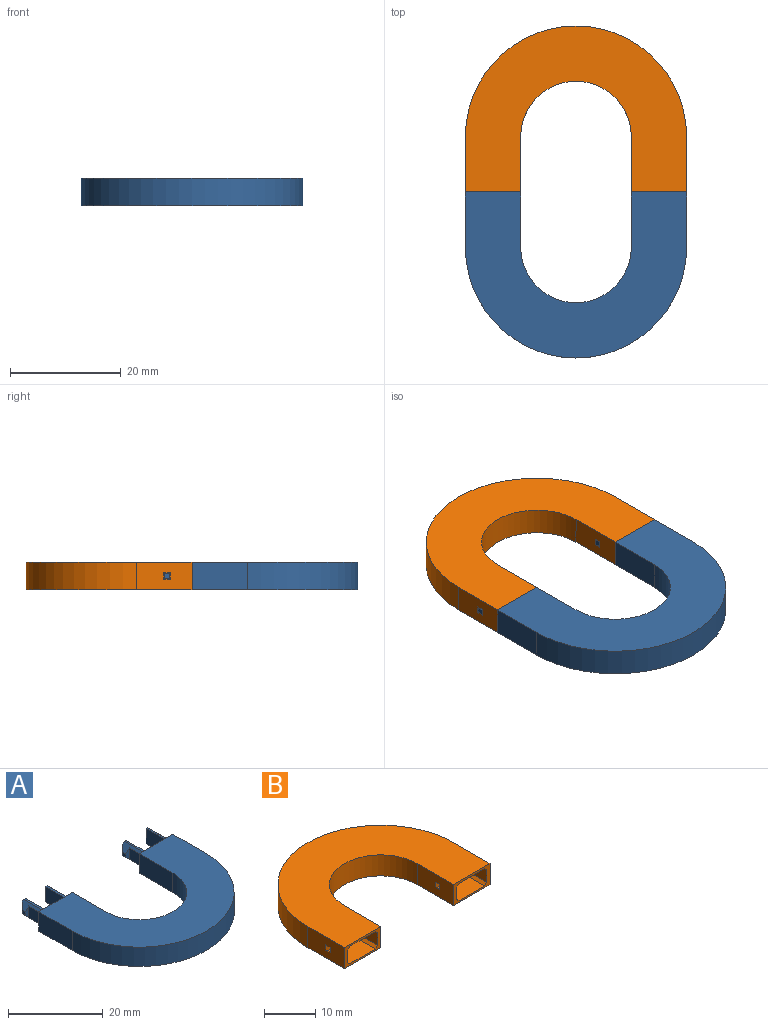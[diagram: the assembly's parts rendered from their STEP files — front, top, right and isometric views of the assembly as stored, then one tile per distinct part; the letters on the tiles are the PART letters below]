
ASSEMBLY  parts=2 mates=1
PART A: 50 faces, bbox 40x36x5 mm
  f0: plane 3.95x1mm, normal (0,1,0), area 3.7mm2, adj f9,f31,f46,f47,f48,f49
  f1: plane 1x1mm, normal (-1,0,0), area 1mm2, adj f9,f10,f47,f49
  f2: plane 1x1mm, normal (1,0,0), area 1mm2, adj f13,f14,f43,f45
  f3: plane 3.95x1mm, normal (0,1,0), area 3.7mm2, adj f14,f32,f42,f43,f44,f45
  f4: plane 3.95x1mm, normal (0,1,0), area 3.7mm2, adj f15,f18,f38,f39,f40,f41
  f5: plane 1x1mm, normal (1,0,0), area 1mm2, adj f17,f18,f38,f40
  f6: plane 1x1mm, normal (-1,0,0), area 1mm2, adj f19,f22,f34,f36
  f7: plane 40x30mm, normal (0,0,1), area 671.2mm2, adj f23,f24,f25,f26,f27,f28,f29,f30
  f8: plane 40x30mm, normal (0,0,-1), area 671.2mm2, adj f23,f24,f25,f26,f27,f28,f29,f30
  f9: plane 2.96x1mm, normal (-0.71,0.71,0), area 2.8mm2, adj f0,f1,f47,f49
  f10: plane 2.96x1mm, normal (0,-1,0), area 2mm2, adj f1,f11,f47,f49
  f11: plane 4x2.96mm, normal (-1,0,0), area 11.9mm2, adj f10,f30,f47,f49
  f12: plane 4x2.96mm, normal (1,0,0), area 11.9mm2, adj f13,f30,f43,f45
  f13: plane 2.96x1mm, normal (0,-1,0), area 2mm2, adj f2,f12,f43,f45
  f14: plane 2.96x1mm, normal (0.71,0.71,0), area 2.8mm2, adj f2,f3,f43,f45
  f15: plane 6x3.95mm, normal (-1,0,0), area 23.7mm2, adj f4,f29,f39,f41
  f16: plane 4x2.96mm, normal (1,0,0), area 11.9mm2, adj f17,f29,f38,f40
  f17: plane 2.96x1mm, normal (0,-1,0), area 2mm2, adj f5,f16,f38,f40
  f18: plane 2.96x1mm, normal (0.71,0.71,0), area 2.8mm2, adj f4,f5,f38,f40
  f19: plane 2.96x1mm, normal (0,-1,0), area 2mm2, adj f6,f20,f34,f36
  f20: plane 4x2.96mm, normal (-1,0,0), area 11.9mm2, adj f19,f29,f34,f36
  f21: plane 6x3.95mm, normal (1,0,0), area 23.7mm2, adj f29,f33,f35,f37
  f22: plane 2.96x1mm, normal (-0.71,0.71,0), area 2.8mm2, adj f6,f33,f34,f36
  f23: cylinder r=20mm len=40mm, axis (0,0,-1), area 314.2mm2, adj f7,f8,f25,f26
  f24: cylinder r=10mm len=20mm, axis (0,0,-1), area 157.1mm2, adj f7,f8,f27,f28
  f25: plane 10x5mm, normal (1,0,0), area 50mm2, adj f7,f8,f23,f29
  f26: plane 10x5mm, normal (-1,0,0), area 50mm2, adj f7,f8,f23,f30
  f27: plane 10x5mm, normal (-1,0,0), area 50mm2, adj f7,f8,f24,f29
  f28: plane 10x5mm, normal (1,0,0), area 50mm2, adj f7,f8,f24,f30
  f29: plane 10x5mm, normal (0,1,0), area 42.6mm2, adj f7,f8,f15,f16,f20,f21,f25,f27
  f30: plane 10x5mm, normal (0,1,0), area 42.6mm2, adj f7,f8,f11,f12,f26,f28,f31,f32
  f31: plane 6x3.95mm, normal (1,0,0), area 23.7mm2, adj f0,f30,f46,f48
  f32: plane 6x3.95mm, normal (-1,0,0), area 23.7mm2, adj f3,f30,f42,f44
  f33: plane 3.95x1mm, normal (0,1,0), area 3.7mm2, adj f21,f22,f34,f35,f36,f37
  f34: plane 6x1.5mm, normal (-0.7,0,0.71), area 6.3mm2, adj f6,f19,f20,f22,f29,f33,f35
  f35: plane 6x0.5mm, normal (0,0,1), area 3mm2, adj f21,f29,f33,f34
  f36: plane 6x1.5mm, normal (-0.7,0,-0.71), area 6.3mm2, adj f6,f19,f20,f22,f29,f33,f37
  f37: plane 6x0.5mm, normal (0,0,-1), area 3mm2, adj f21,f29,f33,f36
  f38: plane 6x1.5mm, normal (0.7,0,0.71), area 6.3mm2, adj f4,f5,f16,f17,f18,f29,f39
  f39: plane 6x0.5mm, normal (0,0,1), area 3mm2, adj f4,f15,f29,f38
  f40: plane 6x1.5mm, normal (0.7,0,-0.71), area 6.3mm2, adj f4,f5,f16,f17,f18,f29,f41
  f41: plane 6x0.5mm, normal (0,0,-1), area 3mm2, adj f4,f15,f29,f40
  f42: plane 6x0.5mm, normal (0,0,-1), area 3mm2, adj f3,f30,f32,f43
  f43: plane 6x1.5mm, normal (0.7,0,-0.71), area 6.3mm2, adj f2,f3,f12,f13,f14,f30,f42
  f44: plane 6x0.5mm, normal (0,0,1), area 3mm2, adj f3,f30,f32,f45
  f45: plane 6x1.5mm, normal (0.7,0,0.71), area 6.3mm2, adj f2,f3,f12,f13,f14,f30,f44
  f46: plane 6x0.5mm, normal (0,0,-1), area 3mm2, adj f0,f30,f31,f47
  f47: plane 6x1.5mm, normal (-0.7,0,-0.71), area 6.3mm2, adj f0,f1,f9,f10,f11,f30,f46
  f48: plane 6x0.5mm, normal (0,0,1), area 3mm2, adj f0,f30,f31,f49
  f49: plane 6x1.5mm, normal (-0.7,0,0.71), area 6.3mm2, adj f0,f1,f9,f10,f11,f30,f48
PART B: 36 faces, bbox 40x30x5 mm
  f0: plane 2.97x0.9mm, normal (0,1,0), area 1.9mm2, adj f1,f5,f6,f7
  f1: plane 3.9x2.97mm, normal (1,0,0), area 11.6mm2, adj f0,f2,f6,f7
  f2: plane 10x5mm, normal (0,-1,0), area 16.7mm2, adj f1,f3,f4,f5,f6,f7,f8,f10
  f3: plane 40x30mm, normal (0,0,-1), area 671.2mm2, adj f2,f5,f10,f13,f14,f19,f26,f27
  f4: plane 40x30mm, normal (0,0,1), area 671.2mm2, adj f2,f5,f10,f13,f14,f19,f26,f27
  f5: plane 10x5mm, normal (-1,0,0), area 48.6mm2, adj f0,f2,f3,f4,f6,f7,f25,f27
  f6: plane 6.1x1.5mm, normal (0.7,0,0.71), area 7.2mm2, adj f0,f1,f2,f5,f23,f25,f29
  f7: plane 6.1x1.5mm, normal (0.7,0,-0.71), area 7.2mm2, adj f0,f1,f2,f5,f23,f25,f31
  f8: plane 3.9x2.97mm, normal (-1,0,0), area 11.6mm2, adj f2,f9,f28,f30
  f9: plane 2.97x0.9mm, normal (0,1,0), area 1.9mm2, adj f8,f10,f28,f30
  f10: plane 10x5mm, normal (1,0,0), area 48.6mm2, adj f2,f3,f4,f9,f24,f26,f28,f30
  f11: plane 2.97x0.9mm, normal (0,1,0), area 1.9mm2, adj f12,f14,f15,f16
  f12: plane 3.9x2.97mm, normal (1,0,0), area 11.6mm2, adj f11,f13,f15,f16
  f13: plane 10x5mm, normal (0,-1,0), area 16.7mm2, adj f3,f4,f12,f14,f15,f16,f17,f19
  f14: plane 10x5mm, normal (-1,0,0), area 48.6mm2, adj f3,f4,f11,f13,f15,f16,f22,f26
  f15: plane 6.1x1.5mm, normal (0.7,0,-0.71), area 7.2mm2, adj f11,f12,f13,f14,f20,f22,f33
  f16: plane 6.1x1.5mm, normal (0.7,0,0.71), area 7.2mm2, adj f11,f12,f13,f14,f20,f22,f35
  f17: plane 3.9x2.97mm, normal (-1,0,0), area 11.6mm2, adj f13,f18,f32,f34
  f18: plane 2.97x0.9mm, normal (0,1,0), area 1.9mm2, adj f17,f19,f32,f34
  f19: plane 10x5mm, normal (1,0,0), area 48.6mm2, adj f3,f4,f13,f18,f21,f27,f32,f34
  f20: plane 8x4.15mm, normal (0,-1,0), area 32.7mm2, adj f15,f16,f21,f22,f32,f33,f34,f35
  f21: plane 3.16x1mm, normal (-0.71,-0.71,0), area 3.1mm2, adj f19,f20,f32,f34
  f22: plane 3.16x1mm, normal (0.71,-0.71,0), area 3.1mm2, adj f14,f15,f16,f20
  f23: plane 8x4.15mm, normal (0,-1,0), area 32.7mm2, adj f6,f7,f24,f25,f28,f29,f30,f31
  f24: plane 3.16x1mm, normal (-0.71,-0.71,0), area 3.1mm2, adj f10,f23,f28,f30
  f25: plane 3.16x1mm, normal (0.71,-0.71,0), area 3.1mm2, adj f5,f6,f7,f23
  f26: cylinder r=10mm len=20mm, axis (0,0,-1), area 157.1mm2, adj f3,f4,f10,f14
  f27: cylinder r=20mm len=40mm, axis (0,0,-1), area 314.2mm2, adj f3,f4,f5,f19
  f28: plane 6.1x1.5mm, normal (-0.7,0,0.71), area 7.2mm2, adj f2,f8,f9,f10,f23,f24,f29
  f29: plane 7x6.1mm, normal (0,0,1), area 42.7mm2, adj f2,f6,f23,f28
  f30: plane 6.1x1.5mm, normal (-0.7,0,-0.71), area 7.2mm2, adj f2,f8,f9,f10,f23,f24,f31
  f31: plane 7x6.1mm, normal (0,0,-1), area 42.7mm2, adj f2,f7,f23,f30
  f32: plane 6.1x1.5mm, normal (-0.7,0,-0.71), area 7.2mm2, adj f13,f17,f18,f19,f20,f21,f33
  f33: plane 7x6.1mm, normal (0,0,-1), area 42.7mm2, adj f13,f15,f20,f32
  f34: plane 6.1x1.5mm, normal (-0.7,0,0.71), area 7.2mm2, adj f13,f17,f18,f19,f20,f21,f35
  f35: plane 7x6.1mm, normal (0,0,1), area 42.7mm2, adj f13,f16,f20,f34
PLACE A t=(-0.64,13.3,2.52)mm
PLACE B t=(-0.64,3.3,2.52)mm
MATE slider A.f29 <-> B.f13  axis (0,1,0) through (14.36,3.3,2.52)mm
